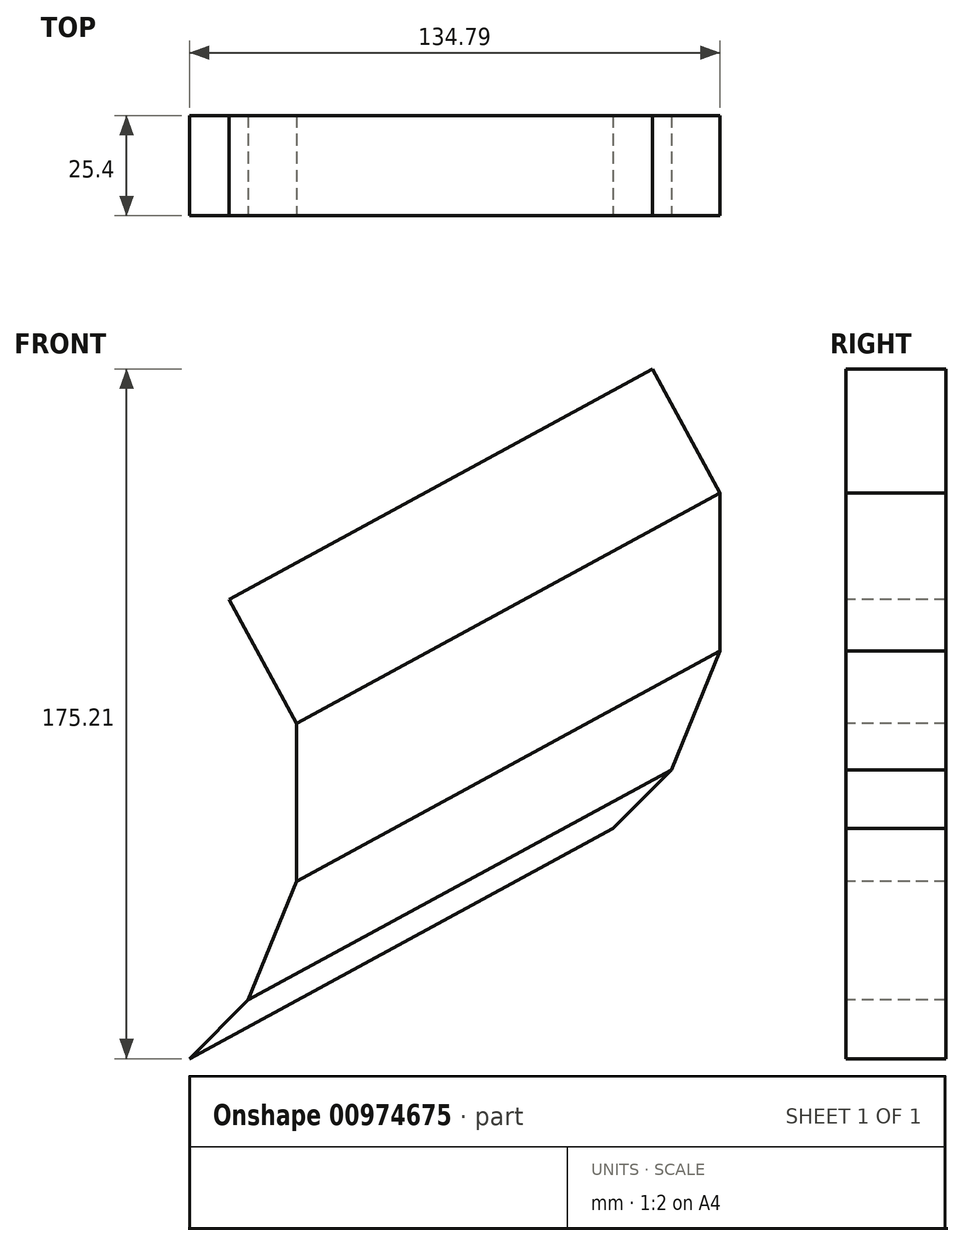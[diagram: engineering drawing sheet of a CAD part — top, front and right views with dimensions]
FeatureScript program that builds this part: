
annotation { "Feature Type Name" : "Feature", "Feature Type Description" : "" }
export const myFeature = defineFeature(function(context is Context, id is Id, definition is map)
    precondition{}
    {
        {
            var Q0;
            Q0=qCreatedBy(makeId("Front.planeOp"),FACE);
            var sketch = newSketch(context, id + "F0", { "sketchPlane" : qUnion([Q0])});
            skLineSegment(sketch, "E0", {"start": v(-47.47, -62.3) * mm, "end": v(-32.65, -47.42) * mm});
            skLineSegment(sketch, "E1", {"start": v(-32.65, -47.42) * mm, "end": v(-20.28, -17.21) * mm});
            skLineSegment(sketch, "E2", {"start": v(-20.28, -17.21) * mm, "end": v(-20.28, 22.89) * mm});
            skLineSegment(sketch, "E3", {"start": v(-20.28, 22.89) * mm, "end": v(-37.41, 54.38) * mm});
            skSolve(sketch);
        }
        {
            var Q0;
            Q0=sQuery(id+"F0.wireOp",EDGE,"E3");
            var Q1;
            Q1=sQuery(id+"F0.wireOp",EDGE,"E2");
            var Q2;
            Q2=sQuery(id+"F0.wireOp",EDGE,"E1");
            var Q3;
            Q3=sQuery(id+"F0.wireOp",EDGE,"E0");
            extrude(context, id + "F1", {"bodyType" : ToolBodyType.SURFACE, "surfaceEntities" : qUnion([Q0, Q1, Q2, Q3]), "depth" : 25.4 * mm, "offsetDistance" : 25.4 * mm});
        }
        {
            var Q0;
            Q0=makeQuery(id+"F1.opExtrude","SWEPT_FACE",FACE,{"disambiguationData":[OSD([sQuery(id+"F0.wireOp",EDGE,"E3")])]});
            var Q1;
            Q1=makeQuery(id+"F1.opExtrude","SWEPT_FACE",FACE,{"disambiguationData":[OSD([sQuery(id+"F0.wireOp",EDGE,"E2")])]});
            var Q2;
            Q2=makeQuery(id+"F1.opExtrude","SWEPT_FACE",FACE,{"disambiguationData":[OSD([sQuery(id+"F0.wireOp",EDGE,"E1")])]});
            var Q3;
            Q3=makeQuery(id+"F1.opExtrude","SWEPT_FACE",FACE,{"disambiguationData":[OSD([sQuery(id+"F0.wireOp",EDGE,"E0")])]});
            extrude(context, id + "F2", {"entities" : qUnion([Q0, Q1, Q2, Q3]), "endBound" : BoundingType.THROUGH_ALL, "depth" : 25.4 * mm, "offsetDistance" : 25.4 * mm});
        }
    });
